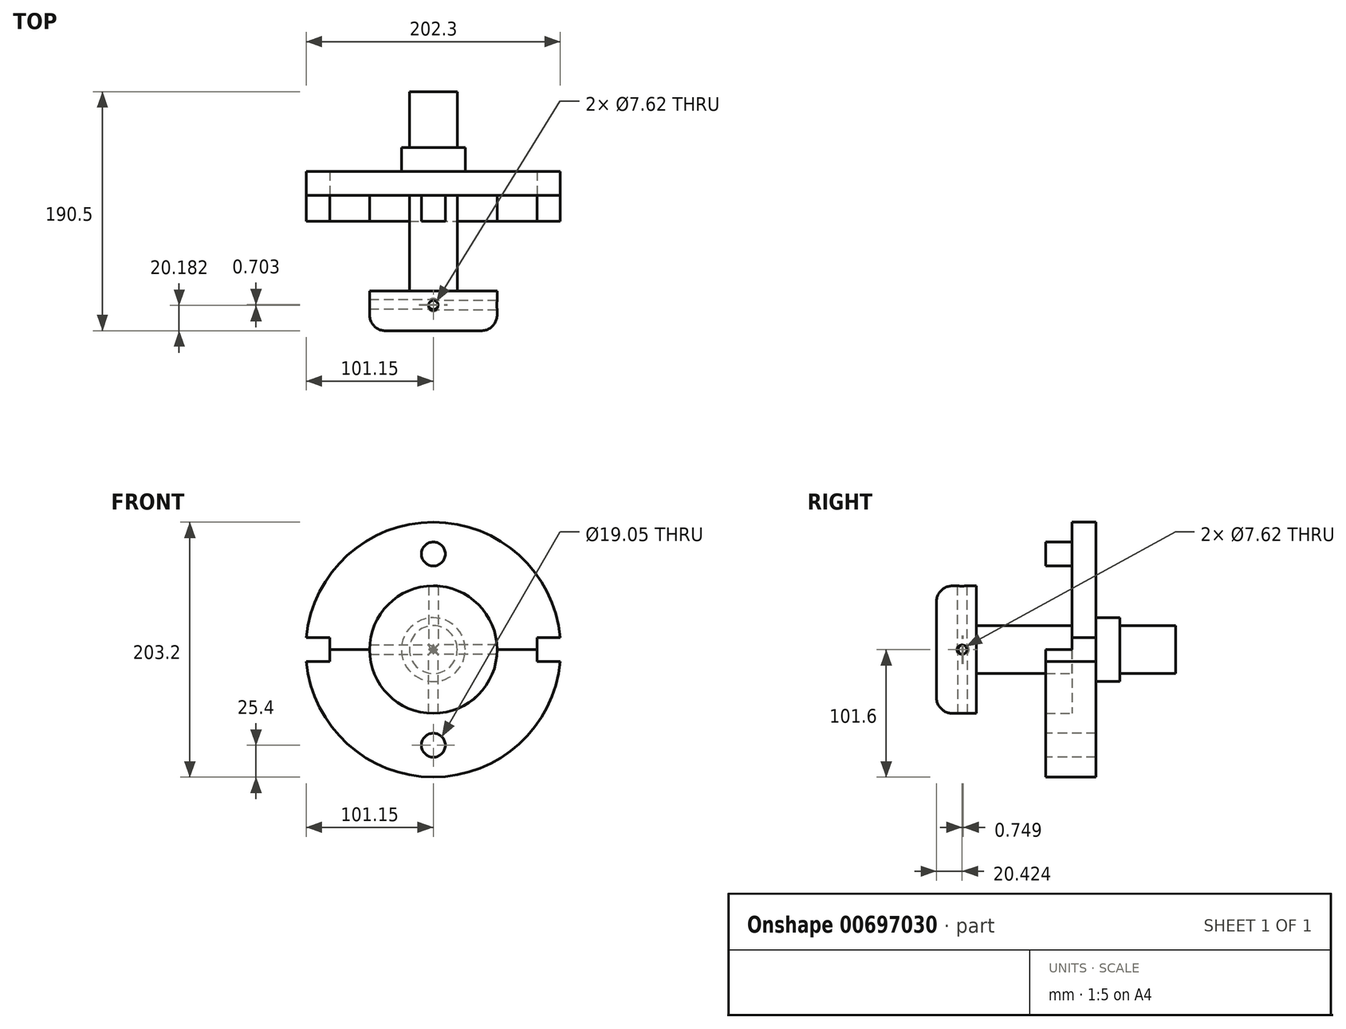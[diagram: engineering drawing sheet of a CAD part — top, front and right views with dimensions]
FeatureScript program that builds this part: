
annotation { "Feature Type Name" : "Feature", "Feature Type Description" : "" }
export const myFeature = defineFeature(function(context is Context, id is Id, definition is map)
    precondition{}
    {
        {
            var Q0;
            Q0=qCreatedBy(makeId("Front.planeOp"),FACE);
            var sketch = newSketch(context, id + "F0", { "sketchPlane" : qUnion([Q0])});
            skCircle(sketch, "E0", {"center": v(0, 0) * mm, "radius": 101.6 * mm});
            skCircle(sketch, "E1", {"center": v(0, 0) * mm, "radius": 76.2 * mm});
            skCircle(sketch, "E2", {"center": v(0, 0) * mm, "radius": 50.8 * mm});
            skCircle(sketch, "E3", {"center": v(0, 0) * mm, "radius": 19.05 * mm});
            skLineSegment(sketch, "E4", {"start": v(0, 0) * mm, "end": v(82.55, 0) * mm});
            skLineSegment(sketch, "E5", {"start": v(82.55, 0) * mm, "end": v(82.55, -9.53) * mm});
            skLineSegment(sketch, "E6", {"start": v(82.55, -9.53) * mm, "end": v(101.15, -9.53) * mm});
            skLineSegment(sketch, "E7", {"start": v(82.55, 0) * mm, "end": v(82.55, 9.53) * mm});
            skLineSegment(sketch, "E8", {"start": v(82.55, 9.53) * mm, "end": v(101.15, 9.53) * mm});
            skLineSegment(sketch, "E9", {"start": v(0, 0) * mm, "end": v(-82.55, 0) * mm});
            skLineSegment(sketch, "E10", {"start": v(-82.55, 0) * mm, "end": v(-82.55, -9.53) * mm});
            skLineSegment(sketch, "E11", {"start": v(-82.55, -9.53) * mm, "end": v(-101.15, -9.53) * mm});
            skLineSegment(sketch, "E12", {"start": v(-82.55, 0) * mm, "end": v(-82.55, 9.52) * mm});
            skLineSegment(sketch, "E13", {"start": v(-82.55, 9.52) * mm, "end": v(-101.15, 9.52) * mm});
            skCircle(sketch, "E14", {"center": v(0, 76.2) * mm, "radius": 9.53 * mm});
            skCircle(sketch, "E15", {"center": v(0, -76.2) * mm, "radius": 9.53 * mm});
            skCircle(sketch, "E16", {"center": v(0, 0) * mm, "radius": 25.4 * mm});
            skSolve(sketch);
        }
        {
            var Q0;
            {var subQ0=sQuery(id+"F0.wireOp",EDGE,"E7");Q0=makeQuery(id+"F0.imprint","IMPRINT",FACE,{"disambiguationData":[TD([[makeQuery(id+"F0.imprint","IMPRINT",EDGE,{"derivedFrom":subQ0}),1.0]])]});}
            var Q1;
            {var subQ5=sQuery(id+"F0.wireOp",EDGE,"E5");Q1=makeQuery(id+"F0.imprint","IMPRINT",FACE,{"disambiguationData":[TD([[makeQuery(id+"F0.imprint","IMPRINT",EDGE,{"derivedFrom":subQ5}),-1.0]])]});}
            var Q2;
            {var subQ1=sQuery(id+"F0.wireOp",EDGE,"E1");var subQ5=sQuery(id+"F0.wireOp",EDGE,"E9");var subQ9=makeQuery(id+"F0.imprint","INTERSECT",VERTEX,{"derivedFrom":[subQ1,subQ5]});Q2=makeQuery(id+"F0.imprint","IMPRINT",FACE,{"disambiguationData":[TD([[makeQuery(id+"F0.imprint","IMPRINT",EDGE,{"disambiguationData":[TD([[subQ9,-1.0]])],"derivedFrom":subQ1}),1.0]])]});}
            var Q3;
            {var subQ0=sQuery(id+"F0.wireOp",EDGE,"E4");var subQ1=sQuery(id+"F0.wireOp",EDGE,"E2");var subQ2=makeQuery(id+"F0.imprint","INTERSECT",VERTEX,{"derivedFrom":[subQ1,subQ0]});Q3=makeQuery(id+"F0.imprint","IMPRINT",FACE,{"disambiguationData":[TD([[makeQuery(id+"F0.imprint","IMPRINT",EDGE,{"disambiguationData":[TD([[subQ2,1.0]])],"derivedFrom":subQ1}),1.0]])]});}
            var Q4;
            {var subQ0=sQuery(id+"F0.wireOp",EDGE,"E4");var subQ1=sQuery(id+"F0.wireOp",EDGE,"E2");var subQ2=makeQuery(id+"F0.imprint","INTERSECT",VERTEX,{"derivedFrom":[subQ1,subQ0]});Q4=makeQuery(id+"F0.imprint","IMPRINT",FACE,{"disambiguationData":[TD([[makeQuery(id+"F0.imprint","IMPRINT",EDGE,{"disambiguationData":[TD([[subQ2,-1.0]])],"derivedFrom":subQ1}),1.0]])]});}
            var Q5;
            {var subQ5=sQuery(id+"F0.wireOp",EDGE,"E1");var subQ7=sQuery(id+"F0.wireOp",EDGE,"E14");var subQ10=makeQuery(id+"F0.imprint","INTERSECT",VERTEX,{"disambiguationData":[OD(0.0)],"derivedFrom":[subQ5,subQ7]});Q5=makeQuery(id+"F0.imprint","IMPRINT",FACE,{"disambiguationData":[TD([[makeQuery(id+"F0.imprint","IMPRINT",EDGE,{"disambiguationData":[TD([[subQ10,1.0]])],"derivedFrom":subQ5}),1.0]])]});}
            var Q6;
            {var subQ0=sQuery(id+"F0.wireOp",EDGE,"E4");var subQ1=sQuery(id+"F0.wireOp",EDGE,"E3");var subQ2=makeQuery(id+"F0.imprint","INTERSECT",VERTEX,{"derivedFrom":[subQ1,subQ0]});Q6=makeQuery(id+"F0.imprint","IMPRINT",FACE,{"disambiguationData":[TD([[makeQuery(id+"F0.imprint","IMPRINT",EDGE,{"disambiguationData":[TD([[subQ2,1.0]])],"derivedFrom":subQ1}),1.0]])]});}
            var Q7;
            {var subQ0=sQuery(id+"F0.wireOp",EDGE,"E4");var subQ1=sQuery(id+"F0.wireOp",EDGE,"E3");var subQ2=makeQuery(id+"F0.imprint","INTERSECT",VERTEX,{"derivedFrom":[subQ1,subQ0]});Q7=makeQuery(id+"F0.imprint","IMPRINT",FACE,{"disambiguationData":[TD([[makeQuery(id+"F0.imprint","IMPRINT",EDGE,{"disambiguationData":[TD([[subQ2,1.0]])],"derivedFrom":subQ1}),1.0]])]});}
            var Q8;
            {var subQ0=sQuery(id+"F0.wireOp",EDGE,"E4");var subQ1=sQuery(id+"F0.wireOp",EDGE,"E3");var subQ2=makeQuery(id+"F0.imprint","INTERSECT",VERTEX,{"derivedFrom":[subQ1,subQ0]});Q8=makeQuery(id+"F0.imprint","IMPRINT",FACE,{"disambiguationData":[TD([[makeQuery(id+"F0.imprint","IMPRINT",EDGE,{"disambiguationData":[TD([[subQ2,-1.0]])],"derivedFrom":subQ1}),1.0]])]});}
            var Q9;
            {var subQ0=sQuery(id+"F0.wireOp",EDGE,"E15");var subQ1=sQuery(id+"F0.wireOp",EDGE,"E1");var subQ2=makeQuery(id+"F0.imprint","INTERSECT",VERTEX,{"disambiguationData":[OD(0.0)],"derivedFrom":[subQ1,subQ0]});Q9=makeQuery(id+"F0.imprint","IMPRINT",FACE,{"disambiguationData":[TD([[makeQuery(id+"F0.imprint","IMPRINT",EDGE,{"disambiguationData":[TD([[subQ2,-1.0]])],"derivedFrom":subQ1}),-1.0]])]});}
            var Q10;
            {var subQ0=sQuery(id+"F0.wireOp",EDGE,"E14");var subQ1=sQuery(id+"F0.wireOp",EDGE,"E1");var subQ2=makeQuery(id+"F0.imprint","INTERSECT",VERTEX,{"disambiguationData":[OD(0.0)],"derivedFrom":[subQ1,subQ0]});Q10=makeQuery(id+"F0.imprint","IMPRINT",FACE,{"disambiguationData":[TD([[makeQuery(id+"F0.imprint","IMPRINT",EDGE,{"disambiguationData":[TD([[subQ2,-1.0]])],"derivedFrom":subQ1}),1.0]])]});}
            var Q11;
            {var subQ0=sQuery(id+"F0.wireOp",EDGE,"E14");var subQ1=sQuery(id+"F0.wireOp",EDGE,"E1");var subQ2=makeQuery(id+"F0.imprint","INTERSECT",VERTEX,{"disambiguationData":[OD(0.0)],"derivedFrom":[subQ1,subQ0]});Q11=makeQuery(id+"F0.imprint","IMPRINT",FACE,{"disambiguationData":[TD([[makeQuery(id+"F0.imprint","IMPRINT",EDGE,{"disambiguationData":[TD([[subQ2,-1.0]])],"derivedFrom":subQ1}),-1.0]])]});}
            var Q12;
            {var subQ0=sQuery(id+"F0.wireOp",EDGE,"E15");var subQ1=sQuery(id+"F0.wireOp",EDGE,"E1");var subQ2=makeQuery(id+"F0.imprint","INTERSECT",VERTEX,{"disambiguationData":[OD(0.0)],"derivedFrom":[subQ1,subQ0]});Q12=makeQuery(id+"F0.imprint","IMPRINT",FACE,{"disambiguationData":[TD([[makeQuery(id+"F0.imprint","IMPRINT",EDGE,{"disambiguationData":[TD([[subQ2,-1.0]])],"derivedFrom":subQ1}),1.0]])]});}
            var Q13;
            {var subQ0=sQuery(id+"F0.wireOp",EDGE,"E4");var subQ1=sQuery(id+"F0.wireOp",EDGE,"E3");var subQ2=makeQuery(id+"F0.imprint","INTERSECT",VERTEX,{"derivedFrom":[subQ1,subQ0]});Q13=makeQuery(id+"F0.imprint","IMPRINT",FACE,{"disambiguationData":[TD([[makeQuery(id+"F0.imprint","IMPRINT",EDGE,{"disambiguationData":[TD([[subQ2,1.0]])],"derivedFrom":subQ1}),-1.0]])]});}
            var Q14;
            {var subQ0=sQuery(id+"F0.wireOp",EDGE,"E4");var subQ1=sQuery(id+"F0.wireOp",EDGE,"E3");var subQ2=makeQuery(id+"F0.imprint","INTERSECT",VERTEX,{"derivedFrom":[subQ1,subQ0]});Q14=makeQuery(id+"F0.imprint","IMPRINT",FACE,{"disambiguationData":[TD([[makeQuery(id+"F0.imprint","IMPRINT",EDGE,{"disambiguationData":[TD([[subQ2,-1.0]])],"derivedFrom":subQ1}),-1.0]])]});}
            extrude(context, id + "F1", {"entities" : qUnion([Q0, Q1, Q2, Q3, Q4, Q5, Q6, Q7, Q8, Q9, Q10, Q11, Q12, Q13, Q14]), "oppositeDirection" : true, "depth" : 19.05 * mm});
        }
        {
            var Q0;
            {var subQ0=sQuery(id+"F0.wireOp",EDGE,"E4");var subQ1=sQuery(id+"F0.wireOp",EDGE,"E3");var subQ2=makeQuery(id+"F0.imprint","INTERSECT",VERTEX,{"derivedFrom":[subQ1,subQ0]});Q0=makeQuery(id+"F0.imprint","IMPRINT",FACE,{"disambiguationData":[TD([[makeQuery(id+"F0.imprint","IMPRINT",EDGE,{"disambiguationData":[TD([[subQ2,-1.0]])],"derivedFrom":subQ1}),1.0]])]});}
            var Q1;
            {var subQ0=sQuery(id+"F0.wireOp",EDGE,"E4");var subQ1=sQuery(id+"F0.wireOp",EDGE,"E3");var subQ2=makeQuery(id+"F0.imprint","INTERSECT",VERTEX,{"derivedFrom":[subQ1,subQ0]});Q1=makeQuery(id+"F0.imprint","IMPRINT",FACE,{"disambiguationData":[TD([[makeQuery(id+"F0.imprint","IMPRINT",EDGE,{"disambiguationData":[TD([[subQ2,1.0]])],"derivedFrom":subQ1}),1.0]])]});}
            extrude(context, id + "F2", {"entities" : qUnion([Q0, Q1]), "operationType" : NewBodyOperationType.ADD, "depth" : 76.2 * mm});
        }
        {
            var Q0;
            {var subQ0=sQuery(id+"F0.wireOp",EDGE,"E15");var subQ1=sQuery(id+"F0.wireOp",EDGE,"E1");var subQ2=makeQuery(id+"F0.imprint","INTERSECT",VERTEX,{"disambiguationData":[OD(0.0)],"derivedFrom":[subQ1,subQ0]});Q0=makeQuery(id+"F0.imprint","IMPRINT",FACE,{"disambiguationData":[TD([[makeQuery(id+"F0.imprint","IMPRINT",EDGE,{"disambiguationData":[TD([[subQ2,-1.0]])],"derivedFrom":subQ1}),1.0]])]});}
            var Q1;
            {var subQ0=sQuery(id+"F0.wireOp",EDGE,"E15");var subQ1=sQuery(id+"F0.wireOp",EDGE,"E1");var subQ2=makeQuery(id+"F0.imprint","INTERSECT",VERTEX,{"disambiguationData":[OD(0.0)],"derivedFrom":[subQ1,subQ0]});Q1=makeQuery(id+"F0.imprint","IMPRINT",FACE,{"disambiguationData":[TD([[makeQuery(id+"F0.imprint","IMPRINT",EDGE,{"disambiguationData":[TD([[subQ2,-1.0]])],"derivedFrom":subQ1}),-1.0]])]});}
            var Q2;
            {var subQ0=sQuery(id+"F0.wireOp",EDGE,"E14");var subQ1=sQuery(id+"F0.wireOp",EDGE,"E1");var subQ2=makeQuery(id+"F0.imprint","INTERSECT",VERTEX,{"disambiguationData":[OD(0.0)],"derivedFrom":[subQ1,subQ0]});Q2=makeQuery(id+"F0.imprint","IMPRINT",FACE,{"disambiguationData":[TD([[makeQuery(id+"F0.imprint","IMPRINT",EDGE,{"disambiguationData":[TD([[subQ2,-1.0]])],"derivedFrom":subQ1}),1.0]])]});}
            var Q3;
            {var subQ0=sQuery(id+"F0.wireOp",EDGE,"E14");var subQ1=sQuery(id+"F0.wireOp",EDGE,"E1");var subQ2=makeQuery(id+"F0.imprint","INTERSECT",VERTEX,{"disambiguationData":[OD(0.0)],"derivedFrom":[subQ1,subQ0]});Q3=makeQuery(id+"F0.imprint","IMPRINT",FACE,{"disambiguationData":[TD([[makeQuery(id+"F0.imprint","IMPRINT",EDGE,{"disambiguationData":[TD([[subQ2,-1.0]])],"derivedFrom":subQ1}),-1.0]])]});}
            extrude(context, id + "F3", {"entities" : qUnion([Q0, Q1, Q2, Q3]), "operationType" : NewBodyOperationType.ADD, "depth" : 20.83 * mm});
        }
        {
            var Q0;
            {var subQ0=sQuery(id+"F0.wireOp",EDGE,"E4");var subQ1=sQuery(id+"F0.wireOp",EDGE,"E3");var subQ2=makeQuery(id+"F0.imprint","INTERSECT",VERTEX,{"derivedFrom":[subQ1,subQ0]});Q0=makeQuery(id+"F0.imprint","IMPRINT",FACE,{"disambiguationData":[TD([[makeQuery(id+"F0.imprint","IMPRINT",EDGE,{"disambiguationData":[TD([[subQ2,-1.0]])],"derivedFrom":subQ1}),-1.0]])]});}
            var Q1;
            {var subQ0=sQuery(id+"F0.wireOp",EDGE,"E4");var subQ1=sQuery(id+"F0.wireOp",EDGE,"E3");var subQ2=makeQuery(id+"F0.imprint","INTERSECT",VERTEX,{"derivedFrom":[subQ1,subQ0]});Q1=makeQuery(id+"F0.imprint","IMPRINT",FACE,{"disambiguationData":[TD([[makeQuery(id+"F0.imprint","IMPRINT",EDGE,{"disambiguationData":[TD([[subQ2,1.0]])],"derivedFrom":subQ1}),-1.0]])]});}
            extrude(context, id + "F4", {"entities" : qUnion([Q0, Q1]), "operationType" : NewBodyOperationType.ADD, "oppositeDirection" : true, "depth" : 38.1 * mm});
        }
        {
            var Q0;
            Q0=makeQuery(id+"F4.boolean.opBoolean","SPLIT",FACE,{"disambiguationData":[TD([makeQuery(id+"F4.opExtrude","SWEPT_FACE",FACE,{"disambiguationData":[OSD([sQuery(id+"F0.wireOp",EDGE,"E3")])]})])],"derivedFrom":makeQuery(id+"F1.opExtrude","CAP_FACE",FACE,{"disambiguationData":[OSD([sQuery(id+"F0.wireOp",EDGE,"E0"),sQuery(id+"F0.wireOp",EDGE,"E5"),sQuery(id+"F0.wireOp",EDGE,"E6"),sQuery(id+"F0.wireOp",EDGE,"E7"),sQuery(id+"F0.wireOp",EDGE,"E8"),sQuery(id+"F0.wireOp",EDGE,"E10"),sQuery(id+"F0.wireOp",EDGE,"E11"),sQuery(id+"F0.wireOp",EDGE,"E12"),sQuery(id+"F0.wireOp",EDGE,"E13")])],"isStart":false})});
            extrude(context, id + "F5", {"entities" : qUnion([Q0]), "operationType" : NewBodyOperationType.ADD, "depth" : 63.5 * mm});
        }
        {
            var Q0;
            Q0=makeQuery(id+"F2.opExtrude","CAP_FACE",FACE,{"disambiguationData":[OSD([sQuery(id+"F0.wireOp",EDGE,"E3")])],"isStart":false});
            var sketch = newSketch(context, id + "F6", { "sketchPlane" : qUnion([Q0])});
            skCircle(sketch, "E17", {"center": v(0, 0) * mm, "radius": 50.8 * mm});
            skSolve(sketch);
        }
        {
            var Q0;
            Q0=makeQuery(id+"F6.imprint","IMPRINT",FACE,{"disambiguationData":[TD([[makeQuery(id+"F6.imprint","IMPRINT",EDGE,{"derivedFrom":sQuery(id+"F6.wireOp",EDGE,"E17")}),1.0]])]});
            var Q1;
            Q1=makeQuery(id+"F6.imprint","IMPRINT",FACE,{"disambiguationData":[TD([[makeQuery(id+"F6.imprint","IMPRINT",EDGE,{"derivedFrom":makeQuery(id+"F2.opExtrude","CAP_EDGE",EDGE,{"disambiguationData":[OSD([sQuery(id+"F0.wireOp",EDGE,"E3")])],"isStart":false})}),1.0]])]});
            extrude(context, id + "F7", {"entities" : qUnion([Q0, Q1]), "operationType" : NewBodyOperationType.ADD, "depth" : 31.75 * mm});
        }
        {
            var Q0;
            Q0=makeQuery(id+"F7.opExtrude","CAP_EDGE",EDGE,{"disambiguationData":[OSD([sQuery(id+"F6.wireOp",EDGE,"E17")])],"isStart":false});
            fillet(context, id + "F8", {"entities" : qUnion([Q0]), "radius" : 12.7 * mm, "tangentPropagation" : true, "allowEdgeOverflow" : false});
        }
        {
            var Q0;
            Q0=qCreatedBy(makeId("Top.planeOp"),FACE);
            var sketch = newSketch(context, id + "F9", { "sketchPlane" : qUnion([Q0])});
            skPoint(sketch, "E18", {"position": v(0, -87.07) * mm});
            skSolve(sketch);
        }
        {
            var Q0;
            Q0=qCreatedBy(makeId("Right.planeOp"),FACE);
            var sketch = newSketch(context, id + "F10", { "sketchPlane" : qUnion([Q0])});
            skPoint(sketch, "E19", {"position": v(-86.78, 0) * mm});
            skSolve(sketch);
        }
        {
            var Q0;
            Q0=sQuery(id+"F10.wireOp",VERTEX,"E19");
            var Q1;
            Q1=makeQuery(id+"F1.opExtrude","SWEPT_BODY",BODY,{"disambiguationData":[OSD([sQuery(id+"F0.wireOp",EDGE,"E0"),sQuery(id+"F0.wireOp",EDGE,"E5"),sQuery(id+"F0.wireOp",EDGE,"E6"),sQuery(id+"F0.wireOp",EDGE,"E7"),sQuery(id+"F0.wireOp",EDGE,"E8"),sQuery(id+"F0.wireOp",EDGE,"E10"),sQuery(id+"F0.wireOp",EDGE,"E11"),sQuery(id+"F0.wireOp",EDGE,"E12"),sQuery(id+"F0.wireOp",EDGE,"E13")])]});
            hole(context, id + "F11", {"style" : HoleStyle.C_SINK, "endStyle" : HoleEndStyle.THROUGH, "holeDiameter" : 7.62 * mm, "cSinkDiameter" : 9.52 * mm, "cSinkAngle" : 90 * degree, "majorDiameter" : 6.35 * mm, "isTappedThrough" : true, "tappedDepth" : 12.7 * mm, "tapClearance" : 3, "locations" : qUnion([Q0]), "scope" : qUnion([Q1])});
        }
        {
            var Q0;
            Q0=sQuery(id+"F9.wireOp",VERTEX,"E18");
            var Q1;
            Q1=makeQuery(id+"F1.opExtrude","SWEPT_BODY",BODY,{"disambiguationData":[OSD([sQuery(id+"F0.wireOp",EDGE,"E0"),sQuery(id+"F0.wireOp",EDGE,"E5"),sQuery(id+"F0.wireOp",EDGE,"E6"),sQuery(id+"F0.wireOp",EDGE,"E7"),sQuery(id+"F0.wireOp",EDGE,"E8"),sQuery(id+"F0.wireOp",EDGE,"E10"),sQuery(id+"F0.wireOp",EDGE,"E11"),sQuery(id+"F0.wireOp",EDGE,"E12"),sQuery(id+"F0.wireOp",EDGE,"E13")])]});
            hole(context, id + "F12", {"style" : HoleStyle.C_SINK, "endStyle" : HoleEndStyle.THROUGH, "holeDiameter" : 7.62 * mm, "cSinkDiameter" : 9.52 * mm, "cSinkAngle" : 90 * degree, "majorDiameter" : 6.35 * mm, "isTappedThrough" : true, "tappedDepth" : 12.7 * mm, "tapClearance" : 3, "locations" : qUnion([Q0]), "scope" : qUnion([Q1])});
        }
        {
            var Q0;
            Q0=qCreatedBy(makeId("Top.planeOp"),FACE);
            var sketch = newSketch(context, id + "F13", { "sketchPlane" : qUnion([Q0])});
            skPoint(sketch, "E20", {"position": v(0, -87.77) * mm});
            skSolve(sketch);
        }
        {
            var Q0;
            Q0=sQuery(id+"F13.wireOp",VERTEX,"E20");
            var Q1;
            Q1=makeQuery(id+"F1.opExtrude","SWEPT_BODY",BODY,{"disambiguationData":[OSD([sQuery(id+"F0.wireOp",EDGE,"E0"),sQuery(id+"F0.wireOp",EDGE,"E5"),sQuery(id+"F0.wireOp",EDGE,"E6"),sQuery(id+"F0.wireOp",EDGE,"E7"),sQuery(id+"F0.wireOp",EDGE,"E8"),sQuery(id+"F0.wireOp",EDGE,"E10"),sQuery(id+"F0.wireOp",EDGE,"E11"),sQuery(id+"F0.wireOp",EDGE,"E12"),sQuery(id+"F0.wireOp",EDGE,"E13")])]});
            hole(context, id + "F14", {"style" : HoleStyle.C_SINK, "endStyle" : HoleEndStyle.THROUGH, "oppositeDirection" : true, "holeDiameter" : 7.62 * mm, "cSinkDiameter" : 9.52 * mm, "cSinkAngle" : 90 * degree, "majorDiameter" : 6.35 * mm, "isTappedThrough" : true, "tappedDepth" : 12.7 * mm, "tapClearance" : 3, "locations" : qUnion([Q0]), "scope" : qUnion([Q1])});
        }
        {
            var Q0;
            Q0=qCreatedBy(makeId("Right.planeOp"),FACE);
            var sketch = newSketch(context, id + "F15", { "sketchPlane" : qUnion([Q0])});
            skPoint(sketch, "E21", {"position": v(-87.53, 0) * mm});
            skSolve(sketch);
        }
        {
            var Q0;
            Q0=sQuery(id+"F15.wireOp",VERTEX,"E21");
            var Q1;
            Q1=makeQuery(id+"F1.opExtrude","SWEPT_BODY",BODY,{"disambiguationData":[OSD([sQuery(id+"F0.wireOp",EDGE,"E0"),sQuery(id+"F0.wireOp",EDGE,"E5"),sQuery(id+"F0.wireOp",EDGE,"E6"),sQuery(id+"F0.wireOp",EDGE,"E7"),sQuery(id+"F0.wireOp",EDGE,"E8"),sQuery(id+"F0.wireOp",EDGE,"E10"),sQuery(id+"F0.wireOp",EDGE,"E11"),sQuery(id+"F0.wireOp",EDGE,"E12"),sQuery(id+"F0.wireOp",EDGE,"E13")])]});
            hole(context, id + "F16", {"style" : HoleStyle.C_SINK, "endStyle" : HoleEndStyle.THROUGH, "oppositeDirection" : true, "holeDiameter" : 7.62 * mm, "cSinkDiameter" : 9.52 * mm, "cSinkAngle" : 90 * degree, "majorDiameter" : 6.35 * mm, "isTappedThrough" : true, "tappedDepth" : 12.7 * mm, "tapClearance" : 3, "locations" : qUnion([Q0]), "scope" : qUnion([Q1])});
        }
    });
